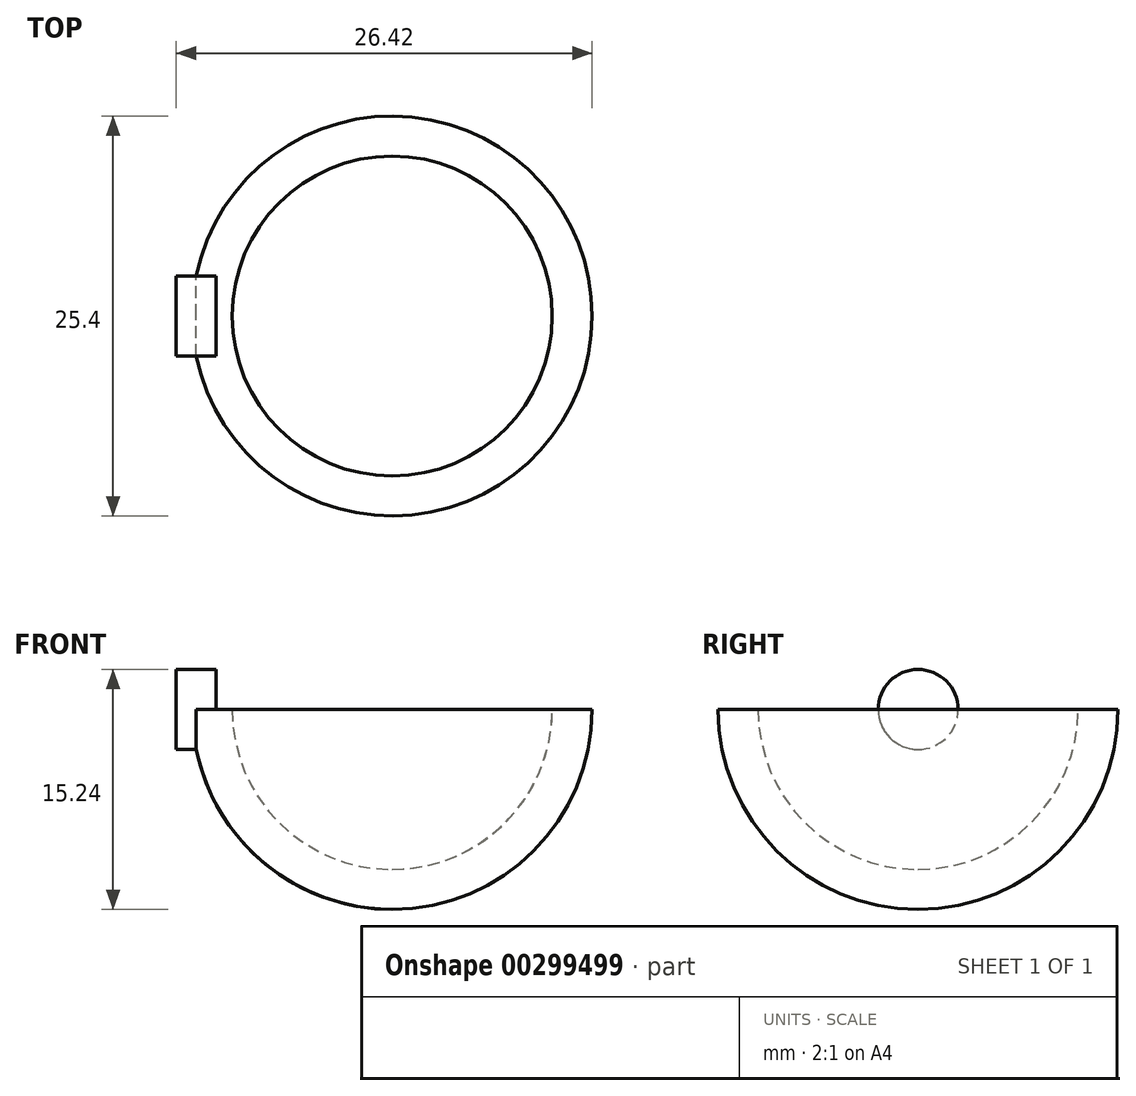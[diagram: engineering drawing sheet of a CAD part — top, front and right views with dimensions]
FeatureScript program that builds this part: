
annotation { "Feature Type Name" : "Feature", "Feature Type Description" : "" }
export const myFeature = defineFeature(function(context is Context, id is Id, definition is map)
    precondition{}
    {
        {
            var Q0;
            Q0=qCreatedBy(makeId("Front.planeOp"),FACE);
            var sketch = newSketch(context, id + "F0", { "sketchPlane" : qUnion([Q0])});
            skArc(sketch, "E0", {"start": v(0, -12.7) * mm, "mid": v(8.98, -8.98) * mm, "end": v(12.7, 0) * mm});
            skLineSegment(sketch, "E1", {"start": v(0, -10.16) * mm, "end": v(0, -12.7) * mm});
            skLineSegment(sketch, "E2", {"start": v(10.16, 0) * mm, "end": v(12.7, 0) * mm});
            skArc(sketch, "E3.0", {"start": v(0, -10.16) * mm, "mid": v(7.18, -7.18) * mm, "end": v(10.16, 0) * mm});
            skSolve(sketch);
        }
        {
            var Q0;
            Q0=makeQuery(id+"F0.imprint","IMPRINT",FACE,{"disambiguationData":[TD([[makeQuery(id+"F0.imprint","IMPRINT",EDGE,{"derivedFrom":sQuery(id+"F0.wireOp",EDGE,"E0")}),1.0]])]});
            var Q1;
            Q1=sQuery(id+"F0.wireOp",EDGE,"E1");
            revolve(context, id + "F1", {"entities" : qUnion([Q0]), "axis" : qUnion([Q1]), "revolveType" : RevolveType.FULL});
        }
        {
            var Q0;
            Q0=qCreatedBy(makeId("Top.planeOp"),FACE);
            var sketch = newSketch(context, id + "F2", { "sketchPlane" : qUnion([Q0])});
            skLineSegment(sketch, "E4", {"start": v(0, 0) * mm, "end": v(-12.7, 0) * mm});
            skSolve(sketch);
        }
        {
            var Q0;
            Q0=sQuery(id+"F2.wireOp",VERTEX,"E4.end");
            var Q1;
            Q1=sQuery(id+"F2.wireOp",EDGE,"E4");
            cPlane(context, id + "F3", {"entities" : qUnion([Q0, Q1]), "cplaneType" : CPlaneType.LINE_POINT, "offset" : 25.4 * mm, "width" : 152.4 * mm, "height" : 152.4 * mm});
        }
        {
            var Q0;
            Q0=qCreatedBy(id+"F3.planeOp",FACE);
            var sketch = newSketch(context, id + "F4", { "sketchPlane" : qUnion([Q0])});
            skCircle(sketch, "E5", {"center": v(0, 0) * mm, "radius": 2.54 * mm});
            skSolve(sketch);
        }
        {
            var Q0;
            Q0=makeQuery(id+"F4.imprint","IMPRINT",FACE,{"disambiguationData":[TD([[makeQuery(id+"F4.imprint","IMPRINT",EDGE,{"derivedFrom":sQuery(id+"F4.wireOp",EDGE,"E5")}),1.0]])]});
            extrude(context, id + "F5", {"entities" : qUnion([Q0]), "operationType" : NewBodyOperationType.ADD, "depth" : 1.02 * mm, "hasSecondDirection" : true, "secondDirectionOppositeDirection" : true, "secondDirectionDepth" : 1.52 * mm});
        }
    });
